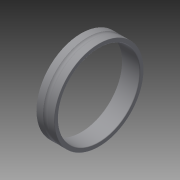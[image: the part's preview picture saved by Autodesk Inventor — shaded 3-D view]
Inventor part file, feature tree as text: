
AUTODESK INVENTOR PART (.ipt)
format: ipt  version: 2014 SP2 (Build 180246200, 246)  size: 153,088 bytes
history: native  units: mm
features: other x14, revolve x1, sketch x1
ambient origin geometry x8: Origin, YZ Plane, XZ Plane, XY Plane, X Axis, Y Axis, Z Axis, Center Point
bodies: Solid1 (feature_tree)
feature tree (16):
  revolve  "Revolution1"  [1 undecoded]
  other  "1_XY"
  other  "1_YZ"
  other  "1_ZX"
  other  "1_X"
  other  "1_Y"
  other  "1_Z"
  other  "1_Center"
  other  "1_Dummy_XY"
  other  "1_Dummy_YZ"
  other  "1_Dummy_ZX"
  other  "1_Dummy_X"
  other  "1_Dummy_Y"
  other  "1_Dummy_Z"
  other  "1_Dummy_Center"
  sketch  "Sketch_1"  dims[d0=360.0deg d1=0.0mm]
note: 1 required parameter value undecoded (feature->parameter linkage not recoverable at this tier; creation-order binding heuristic only, values carry confidence <= 0.55)
